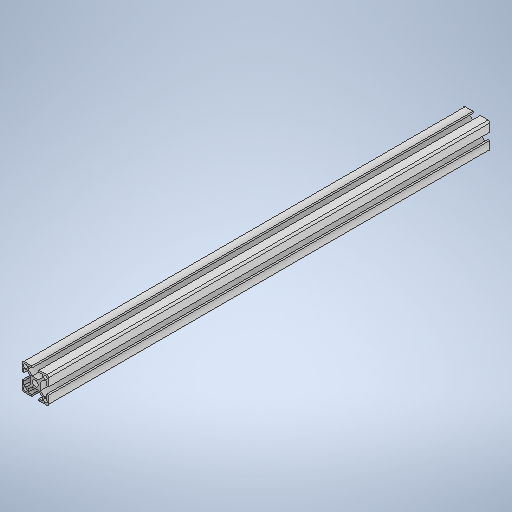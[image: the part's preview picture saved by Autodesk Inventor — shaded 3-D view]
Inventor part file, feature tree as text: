
AUTODESK INVENTOR PART (.ipt)
format: ipt  version: 2025 (Build 290162000, 162)  size: 314,368 bytes
history: native  units: in
note: dims shown in document units (in); Inventor stores cm internally (conversion verified against a paired STEP export)
features: extrude x1, sketch x1
ambient origin geometry x8: Origin, YZ Plane, XZ Plane, XY Plane, X Axis, Y Axis, Z Axis, Center Point
bodies: Solid1 (feature_tree)
feature tree (2):
  extrude  "Extrusion1"  Depth=19.685in
  sketch  "Sketch1"  dims[d6=19.685in d7=0.0in d8=0.1969in d9=0.0344in]
